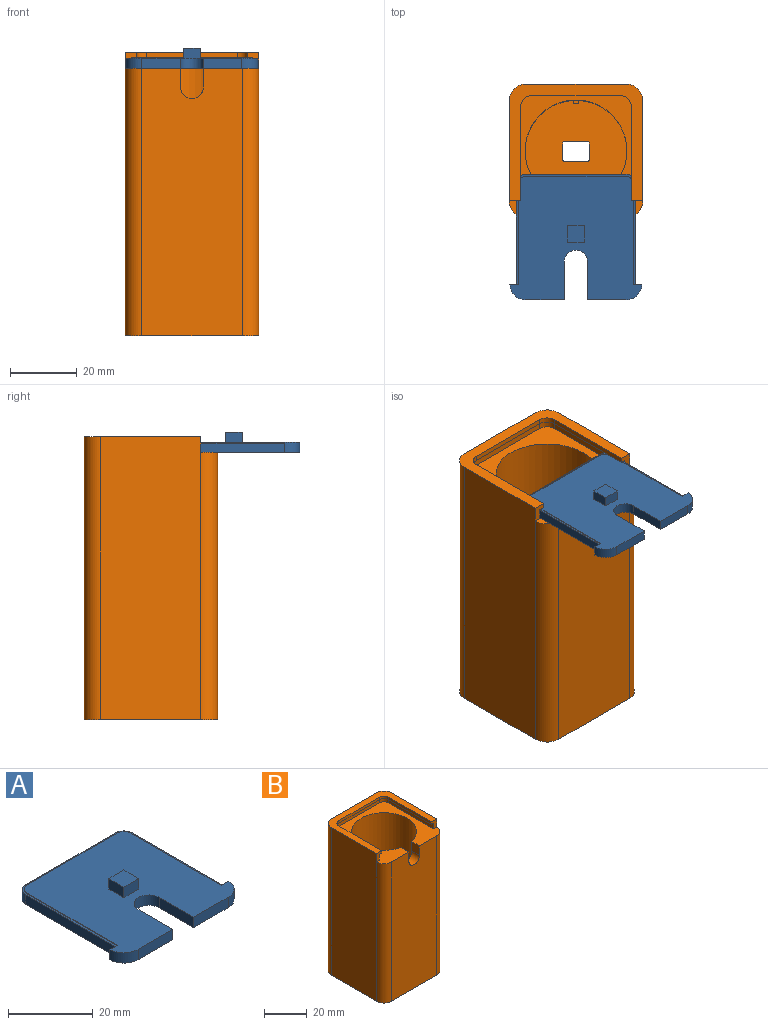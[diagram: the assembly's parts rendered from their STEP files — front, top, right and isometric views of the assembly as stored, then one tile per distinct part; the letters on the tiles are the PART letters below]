
ASSEMBLY  parts=2 mates=1
PART A: 27 faces, bbox 39.6x37.6x6 mm
  f0: plane 11.51x3mm, normal (0,-1,0), area 34.5mm2, adj f1,f2,f3,f25
  f1: plane 39.59x37.1mm, normal (0,0,1), area 1170.1mm2, adj f0,f3,f4,f10,f11,f12,f13,f14
  f2: plane 39.59x37.6mm, normal (0,0,-1), area 1244.7mm2, adj f0,f3,f4,f5,f6,f7,f8,f9
  f3: cylinder r=4.8mm len=4.8mm, axis (0,0,1), area 22mm2, adj f0,f1,f2,f4
  f4: plane 3x2.5mm, normal (0,1,0), area 6.1mm2, adj f1,f2,f3,f5,f13,f18
  f5: plane 30.2x2.8mm, normal (-1,0,0), area 84.6mm2, adj f2,f4,f6,f18
  f6: cylinder r=2.8mm len=2.8mm, axis (0,0,1), area 12.3mm2, adj f2,f5,f7,f18
  f7: plane 30x2.8mm, normal (0,1,0), area 84mm2, adj f2,f6,f8,f18
  f8: cylinder r=2.8mm len=2.8mm, axis (0,0,1), area 12.3mm2, adj f2,f7,f9,f18
  f9: plane 30.2x2.8mm, normal (1,0,0), area 84.6mm2, adj f2,f8,f10,f18
  f10: plane 3x2.5mm, normal (0,1,0), area 6.1mm2, adj f1,f2,f9,f11,f17,f18
  f11: cylinder r=4.8mm len=4.8mm, axis (0,0,1), area 22mm2, adj f1,f2,f10,f12
  f12: plane 11.5x3mm, normal (0,-1,0), area 34.5mm2, adj f1,f2,f11,f26
  f13: plane 30x0.2mm, normal (-1,0,0), area 6mm2, adj f1,f4,f14,f18
  f14: cylinder r=2.5mm len=2.5mm, axis (0,0,1), area 0.8mm2, adj f1,f13,f15,f18
  f15: plane 29.6x0.2mm, normal (0,1,0), area 5.9mm2, adj f1,f14,f16,f18
  f16: cylinder r=2.5mm len=2.5mm, axis (0,0,1), area 0.8mm2, adj f1,f15,f17,f18
  f17: plane 30x0.2mm, normal (1,0,0), area 6mm2, adj f1,f10,f16,f18
  f18: plane 35.6x33mm, normal (0,0,1), area 49.6mm2, adj f4,f5,f6,f7,f8,f9,f10,f13
  f19: plane 5x3mm, normal (0,-1,0), area 15mm2, adj f1,f20,f22,f23
  f20: plane 5x3mm, normal (1,0,0), area 15mm2, adj f1,f19,f21,f23
  f21: plane 5x3mm, normal (0,1,0), area 15mm2, adj f1,f20,f22,f23
  f22: plane 5x3mm, normal (-1,0,0), area 15mm2, adj f1,f19,f21,f23
  f23: plane 5x5mm, normal (0,0,1), area 25mm2, adj f19,f20,f21,f22
  f24: cylinder r=3.5mm len=7mm, axis (0,0,1), area 33.6mm2, adj f1,f2,f25,f26
  f25: plane 11.21x3mm, normal (1,0,0), area 33.6mm2, adj f0,f1,f2,f24
  f26: plane 11.4x3mm, normal (-1,0,0), area 34.2mm2, adj f1,f2,f12,f24
PART B: 41 faces, bbox 40x40x84.8 mm
  f0: cylinder r=15.25mm len=78mm, axis (0,0,1), area 7370.6mm2, adj f1,f11,f20,f21,f22,f24,f25,f26
  f1: plane 30.5x30.48mm, normal (0,0,1), area 681.3mm2, adj f0,f12,f13,f14,f15,f16,f17,f18
  f2: plane 40x40mm, normal (0,0,-1), area 1530.8mm2, adj f3,f4,f5,f6,f7,f8,f9,f10
  f3: plane 84.75x30mm, normal (-1,0,0), area 2542.5mm2, adj f2,f4,f10,f27,f40
  f4: cylinder r=5mm len=80mm, axis (0,0,-1), area 628.3mm2, adj f2,f3,f5,f11
  f5: plane 80x30mm, normal (0,-1,0), area 2342.3mm2, adj f2,f4,f6,f11,f24,f25,f26
  f6: cylinder r=5mm len=80mm, axis (0,0,-1), area 628.3mm2, adj f2,f5,f7,f11
  f7: plane 84.75x30mm, normal (1,0,0), area 2542.5mm2, adj f2,f6,f8,f33,f40
  f8: cylinder r=5mm len=84.75mm, axis (0,0,-1), area 665.6mm2, adj f2,f7,f9,f40
  f9: plane 84.75x30mm, normal (0,1,0), area 2542.5mm2, adj f2,f8,f10,f40
  f10: cylinder r=5mm len=84.75mm, axis (0,0,-1), area 665.6mm2, adj f2,f3,f9,f40
  f11: plane 40x38mm, normal (0,0,1), area 608.6mm2, adj f0,f4,f5,f6,f25,f26,f27,f28
  f12: plane 5x2mm, normal (-1,0,0), area 10mm2, adj f1,f2,f13,f19
  f13: cylinder r=0.5mm len=2mm, axis (0,0,-1), area 1.6mm2, adj f1,f2,f12,f14
  f14: plane 7x2mm, normal (0,1,0), area 14mm2, adj f1,f2,f13,f15
  f15: cylinder r=0.5mm len=2mm, axis (0,0,-1), area 1.6mm2, adj f1,f2,f14,f16
  f16: plane 5x2mm, normal (1,0,0), area 10mm2, adj f1,f2,f15,f17
  f17: cylinder r=0.5mm len=2mm, axis (0,0,-1), area 1.6mm2, adj f1,f2,f16,f18
  f18: plane 7x2mm, normal (0,-1,0), area 14mm2, adj f1,f2,f17,f19
  f19: cylinder r=0.5mm len=2mm, axis (0,0,-1), area 1.6mm2, adj f1,f2,f12,f18
  f20: plane 30x0.98mm, normal (-1,0,0), area 29.4mm2, adj f0,f1,f22,f23
  f21: plane 30x0.98mm, normal (1,0,0), area 29.4mm2, adj f0,f1,f22,f23
  f22: plane 1.5x1mm, normal (0,0,1), area 1.5mm2, adj f0,f20,f21,f23
  f23: plane 30x1.5mm, normal (0,-1,0), area 45mm2, adj f1,f20,f21,f22
  f24: cylinder r=3.5mm len=7mm, axis (0,-1,0), area 54.5mm2, adj f0,f5,f25,f26
  f25: plane 5.5x5.16mm, normal (1,0,0), area 28.4mm2, adj f0,f5,f11,f24
  f26: plane 5.5x5.16mm, normal (-1,0,0), area 28.4mm2, adj f0,f5,f11,f24
  f27: plane 4.75x3.5mm, normal (0,-1,0), area 11.8mm2, adj f3,f11,f28,f34,f35,f40
  f28: plane 30x3.25mm, normal (1,0,0), area 97.5mm2, adj f11,f27,f29,f34
  f29: cylinder r=3mm len=3.25mm, axis (0,0,-1), area 15.3mm2, adj f11,f28,f30,f34
  f30: plane 30x3.25mm, normal (0,-1,0), area 97.5mm2, adj f11,f29,f31,f34
  f31: cylinder r=3mm len=3.25mm, axis (0,0,-1), area 15.3mm2, adj f11,f30,f32,f34
  f32: plane 30x3.25mm, normal (-1,0,0), area 97.5mm2, adj f11,f31,f33,f34
  f33: plane 4.75x3.5mm, normal (0,-1,0), area 11.8mm2, adj f7,f11,f32,f34,f39,f40
  f34: plane 36x33mm, normal (0,0,-1), area 148.5mm2, adj f27,f28,f29,f30,f31,f32,f33,f35
  f35: plane 28.5x1.5mm, normal (1,0,0), area 42.8mm2, adj f27,f34,f36,f40
  f36: cylinder r=3mm len=3mm, axis (0,0,-1), area 7.1mm2, adj f34,f35,f37,f40
  f37: plane 27x1.5mm, normal (0,-1,0), area 40.5mm2, adj f34,f36,f38,f40
  f38: cylinder r=3mm len=3mm, axis (0,0,-1), area 7.1mm2, adj f34,f37,f39,f40
  f39: plane 28.5x1.5mm, normal (-1,0,0), area 42.8mm2, adj f33,f34,f38,f40
  f40: plane 40x35mm, normal (0,0,1), area 353.6mm2, adj f3,f7,f8,f9,f10,f27,f33,f35
PLACE A t=(-0.03,-24.85,-7.01)mm
PLACE B t=(0,0,1.39)mm fixed
MATE planar A.f2 <-> B.f11  axis (0,0,-1) through (-0.03,-25.07,81.39)mm
